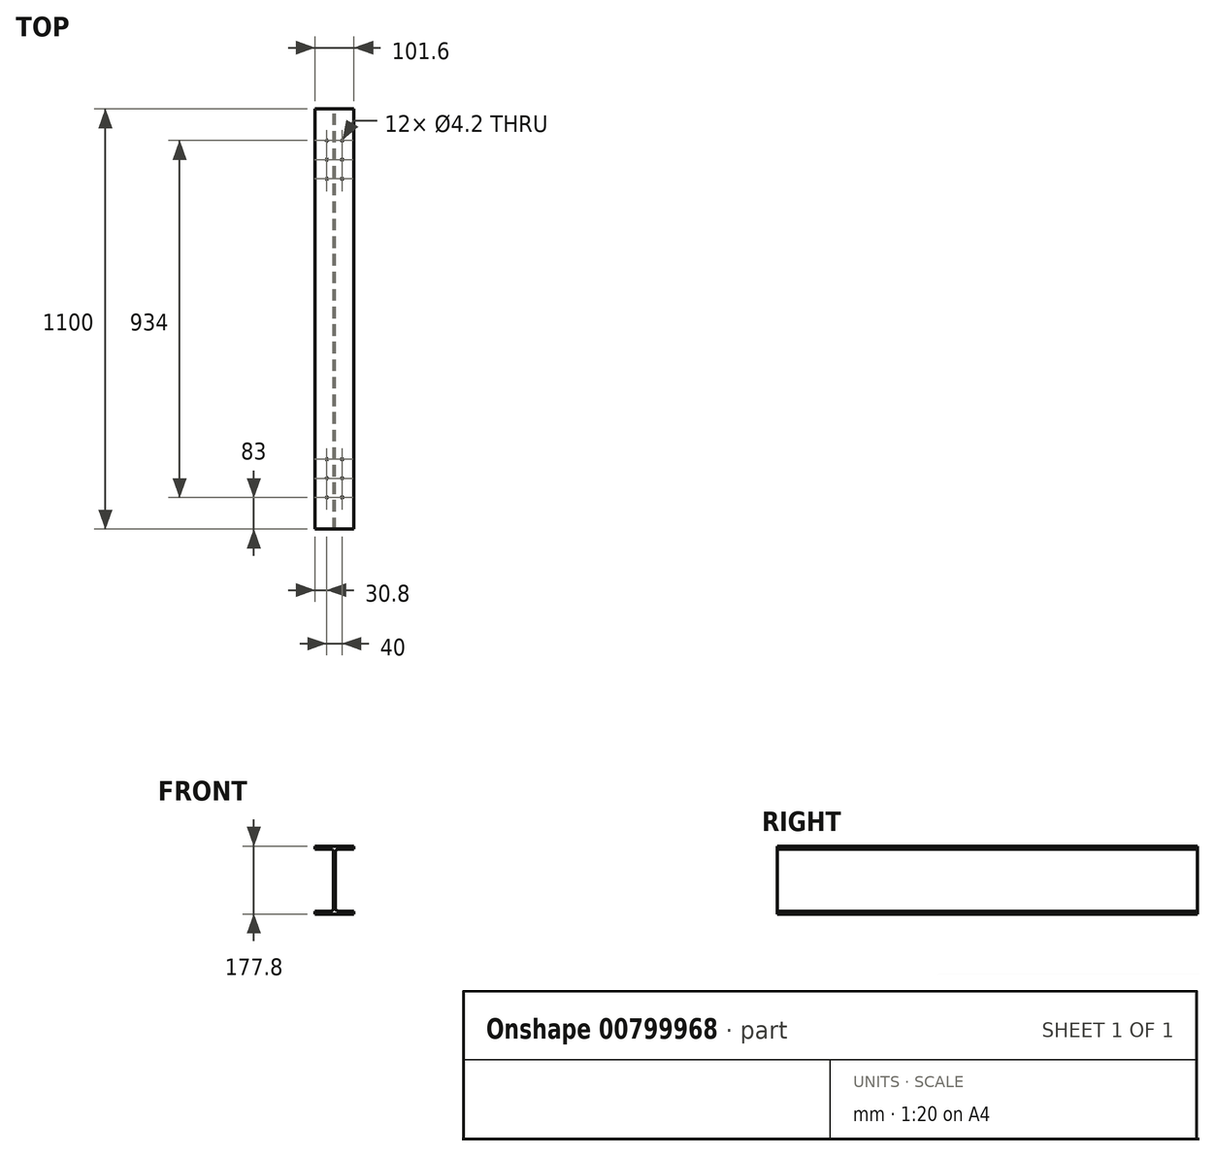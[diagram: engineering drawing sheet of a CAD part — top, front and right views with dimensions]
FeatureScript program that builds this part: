
annotation { "Feature Type Name" : "Feature", "Feature Type Description" : "" }
export const myFeature = defineFeature(function(context is Context, id is Id, definition is map)
    precondition{}
    {
        {
            var Q0;
            Q0=qCreatedBy(makeId("Front.planeOp"),FACE);
            var sketch = newSketch(context, id + "F0", { "sketchPlane" : qUnion([Q0])});
            skLineSegment(sketch, "E0", {"start": v(-50.8, -35.6) * mm, "end": v(-50.8, -43.5) * mm});
            skLineSegment(sketch, "E1", {"start": v(-50.8, -43.5) * mm, "end": v(0, -43.5) * mm});
            skLineSegment(sketch, "E2", {"start": v(0, -43.5) * mm, "end": v(0, 134.3) * mm});
            skLineSegment(sketch, "E3", {"start": v(0, 134.3) * mm, "end": v(-50.8, 134.3) * mm});
            skLineSegment(sketch, "E4", {"start": v(-50.8, 134.3) * mm, "end": v(-50.8, 126.4) * mm});
            skLineSegment(sketch, "E5", {"start": v(-50.8, 126.4) * mm, "end": v(-9.95, 126.4) * mm});
            skLineSegment(sketch, "E6", {"start": v(-2.35, 118.8) * mm, "end": v(-2.35, -28) * mm});
            skLineSegment(sketch, "E7", {"start": v(-9.95, -35.6) * mm, "end": v(-50.8, -35.6) * mm});
            skPoint(sketch, "E8.visualSharp", {"position": v(-2.35, 126.4) * mm});
            skArc(sketch, "E8.filletArc", {"start": v(-2.35, 118.8) * mm, "mid": v(-4.58, 124.18) * mm, "end": v(-9.95, 126.4) * mm});
            skPoint(sketch, "E9.visualSharp", {"position": v(-2.35, -35.6) * mm});
            skArc(sketch, "E9.filletArc", {"start": v(-9.95, -35.6) * mm, "mid": v(-4.58, -33.37) * mm, "end": v(-2.35, -28) * mm});
            skLineSegment(sketch, "E10.MirrorCS", {"start": v(0, 134.3) * mm, "end": v(50.8, 134.3) * mm});
            skLineSegment(sketch, "E11.MirrorCS", {"start": v(50.8, 134.3) * mm, "end": v(50.8, 126.4) * mm});
            skLineSegment(sketch, "E12.MirrorCS", {"start": v(50.8, 126.4) * mm, "end": v(9.95, 126.4) * mm});
            skPoint(sketch, "E13.MirrorP", {"position": v(2.35, 126.4) * mm});
            skArc(sketch, "E14.MirrorCS", {"start": v(2.35, 118.8) * mm, "mid": v(4.58, 124.18) * mm, "end": v(9.95, 126.4) * mm});
            skLineSegment(sketch, "E15.MirrorCS", {"start": v(2.35, 118.8) * mm, "end": v(2.35, -28) * mm});
            skPoint(sketch, "E16.MirrorP", {"position": v(2.35, -35.6) * mm});
            skArc(sketch, "E17.MirrorCS", {"start": v(9.95, -35.6) * mm, "mid": v(4.58, -33.37) * mm, "end": v(2.35, -28) * mm});
            skLineSegment(sketch, "E18.MirrorCS", {"start": v(9.95, -35.6) * mm, "end": v(50.8, -35.6) * mm});
            skLineSegment(sketch, "E19.MirrorCS", {"start": v(50.8, -35.6) * mm, "end": v(50.8, -43.5) * mm});
            skLineSegment(sketch, "E20.MirrorCS", {"start": v(50.8, -43.5) * mm, "end": v(0, -43.5) * mm});
            skSolve(sketch);
        }
        {
            var Q0;
            Q0 = qSketchRegion(id + "F0", true);
            extrude(context, id + "F1", {"entities" : qUnion([Q0]), "depth" : 1100 * mm, "offsetDistance" : 25 * mm});
        }
        {
            var Q0;
            Q0=makeQuery(id+"F1.opExtrude","SWEPT_FACE",FACE,{"disambiguationData":[OSD([sQuery(id+"F0.wireOp",EDGE,"E3"),sQuery(id+"F0.wireOp",EDGE,"E10.MirrorCS")])]});
            var sketch = newSketch(context, id + "F2", { "sketchPlane" : qUnion([Q0])});
            skLineSegment(sketch, "E21", {"start": v(0, 0) * mm, "end": v(0, -1100) * mm, "construction": true});
            skLineSegment(sketch, "E22", {"start": v(0, -1100) * mm, "end": v(278.55, -1100) * mm, "construction": true});
            skLineSegment(sketch, "E23", {"start": v(0, 0) * mm, "end": v(316.98, 0) * mm, "construction": true});
            skLineSegment(sketch, "E24", {"start": v(-536.83, -550) * mm, "end": v(765.22, -550) * mm, "construction": true});
            skPoint(sketch, "E24.startSnap0", {"position": v(0, -550) * mm});
            skLineSegment(sketch, "E25", {"start": v(-536.83, -183) * mm, "end": v(726.8, -183) * mm, "construction": true});
            skLineSegment(sketch, "E26", {"start": v(-20, 0) * mm, "end": v(-20, -266) * mm, "construction": true});
            skLineSegment(sketch, "E27", {"start": v(20, -285.71) * mm, "end": v(20, 0) * mm, "construction": true});
            skPoint(sketch, "E28", {"position": v(-20, -183) * mm});
            skPoint(sketch, "E29", {"position": v(-20, -133) * mm});
            skPoint(sketch, "E30", {"position": v(-20, -83) * mm});
            skPoint(sketch, "E31.MirrorP", {"position": v(20, -83) * mm});
            skPoint(sketch, "E32.MirrorP", {"position": v(20, -133) * mm});
            skPoint(sketch, "E33.MirrorP", {"position": v(20, -183) * mm});
            skLineSegment(sketch, "E34.MirrorCS", {"start": v(-536.83, -917) * mm, "end": v(726.8, -917) * mm, "construction": true});
            skLineSegment(sketch, "E35.MirrorCS", {"start": v(20, -814.29) * mm, "end": v(20, -1100) * mm, "construction": true});
            skLineSegment(sketch, "E36.MirrorCS", {"start": v(-20, -1100) * mm, "end": v(-20, -834) * mm, "construction": true});
            skPoint(sketch, "E37.MirrorP", {"position": v(-20, -917) * mm});
            skPoint(sketch, "E38.MirrorP", {"position": v(20, -917) * mm});
            skPoint(sketch, "E39.MirrorP", {"position": v(20, -967) * mm});
            skPoint(sketch, "E40.MirrorP", {"position": v(-20, -967) * mm});
            skPoint(sketch, "E41.MirrorP", {"position": v(-20, -1017) * mm});
            skPoint(sketch, "E42.MirrorP", {"position": v(20, -1017) * mm});
            skSolve(sketch);
        }
        {
            var Q0;
            Q0=sQuery(id+"F2.wireOp",VERTEX,"E41.MirrorP");
            var Q1;
            Q1=sQuery(id+"F2.wireOp",VERTEX,"E40.MirrorP");
            var Q2;
            Q2=sQuery(id+"F2.wireOp",VERTEX,"E37.MirrorP");
            var Q3;
            Q3=sQuery(id+"F2.wireOp",VERTEX,"E38.MirrorP");
            var Q4;
            Q4=sQuery(id+"F2.wireOp",VERTEX,"E39.MirrorP");
            var Q5;
            Q5=sQuery(id+"F2.wireOp",VERTEX,"E42.MirrorP");
            var Q6;
            Q6=sQuery(id+"F2.wireOp",VERTEX,"E28");
            var Q7;
            Q7=sQuery(id+"F2.wireOp",VERTEX,"E29");
            var Q8;
            Q8=sQuery(id+"F2.wireOp",VERTEX,"E30");
            var Q9;
            Q9=sQuery(id+"F2.wireOp",VERTEX,"E31.MirrorP");
            var Q10;
            Q10=sQuery(id+"F2.wireOp",VERTEX,"E32.MirrorP");
            var Q11;
            Q11=sQuery(id+"F2.wireOp",VERTEX,"E33.MirrorP");
            var Q12;
            Q12=makeQuery(id+"F1.opExtrude","SWEPT_BODY",BODY,{"disambiguationData":[OSD([sQuery(id+"F0.wireOp",EDGE,"E0"),sQuery(id+"F0.wireOp",EDGE,"E1"),sQuery(id+"F0.wireOp",EDGE,"E3"),sQuery(id+"F0.wireOp",EDGE,"E4"),sQuery(id+"F0.wireOp",EDGE,"E5"),sQuery(id+"F0.wireOp",EDGE,"E6"),sQuery(id+"F0.wireOp",EDGE,"E7"),sQuery(id+"F0.wireOp",EDGE,"E8.filletArc"),sQuery(id+"F0.wireOp",EDGE,"E9.filletArc"),sQuery(id+"F0.wireOp",EDGE,"E10.MirrorCS"),sQuery(id+"F0.wireOp",EDGE,"E11.MirrorCS"),sQuery(id+"F0.wireOp",EDGE,"E12.MirrorCS"),sQuery(id+"F0.wireOp",EDGE,"E14.MirrorCS"),sQuery(id+"F0.wireOp",EDGE,"E15.MirrorCS"),sQuery(id+"F0.wireOp",EDGE,"E17.MirrorCS"),sQuery(id+"F0.wireOp",EDGE,"E18.MirrorCS"),sQuery(id+"F0.wireOp",EDGE,"E19.MirrorCS"),sQuery(id+"F0.wireOp",EDGE,"E20.MirrorCS")])]});
            hole(context, id + "F3", {"style" : HoleStyle.SIMPLE, "endStyle" : HoleEndStyle.BLIND, "standardTappedOrClearance" : lookupTablePath({ "standard" : "ISO", "engagement" : "75%", "pitch" : "0.8 mm", "size" : "M5", "type" : "Tapped" }), "standardBlindInLast" : lookupTablePath({ "standard" : "ISO", "engagement" : "75%", "pitch" : "0.8 mm", "size" : "M5", "type" : "Tapped" }), "holeDiameter" : 4.2 * mm, "majorDiameter" : 5 * mm, "showTappedDepth" : true, "holeDepth" : 50 * mm, "isTappedThrough" : true, "tappedDepth" : 47.6 * mm, "tapClearance" : 3, "locations" : qUnion([Q0, Q1, Q2, Q3, Q4, Q5, Q6, Q7, Q8, Q9, Q10, Q11]), "scope" : qUnion([Q12])});
        }
    });
